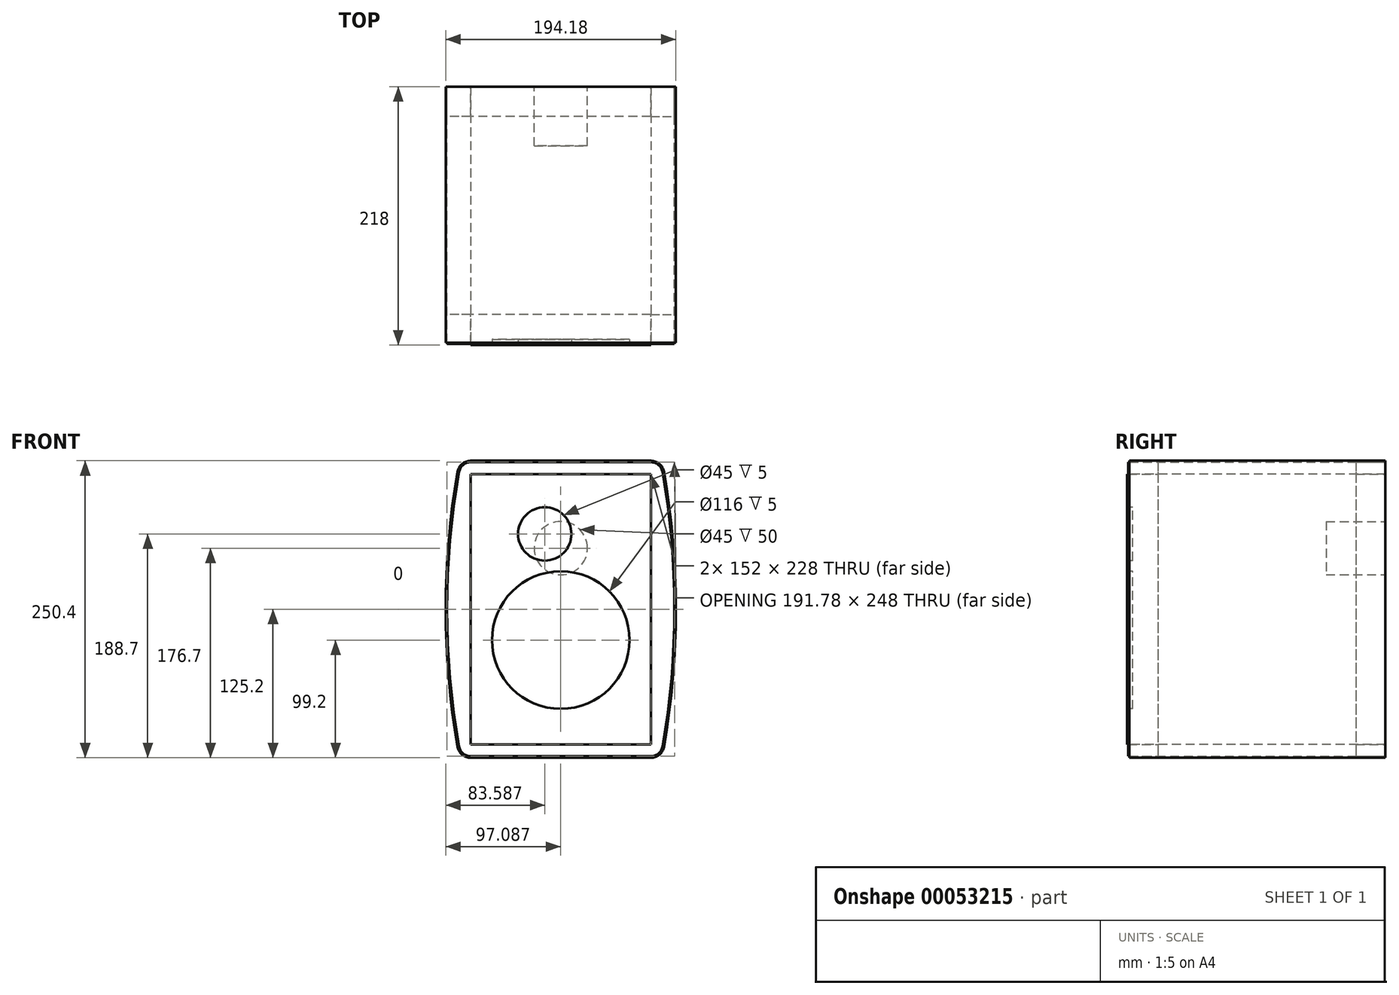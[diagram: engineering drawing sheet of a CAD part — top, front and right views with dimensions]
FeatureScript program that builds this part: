
annotation { "Feature Type Name" : "Feature", "Feature Type Description" : "" }
export const myFeature = defineFeature(function(context is Context, id is Id, definition is map)
    precondition{}
    {
        {
            var Q0;
            Q0=qCreatedBy(makeId("Top.planeOp"),FACE);
            var sketch = newSketch(context, id + "F0", { "sketchPlane" : qUnion([Q0])});
            skLineSegment(sketch, "E0.bottom", {"start": v(-73.3, 36.27) * mm, "end": v(78.7, 36.27) * mm});
            skLineSegment(sketch, "E0.top", {"start": v(-73.3, -181.73) * mm, "end": v(78.7, -181.73) * mm});
            skLineSegment(sketch, "E0.left", {"start": v(-73.3, 36.27) * mm, "end": v(-73.3, -181.73) * mm});
            skLineSegment(sketch, "E0.right", {"start": v(78.7, 36.27) * mm, "end": v(78.7, -181.73) * mm});
            skSolve(sketch);
        }
        {
            var Q0;
            Q0 = qSketchRegion(id + "F0", true);
            extrude(context, id + "F1", {"entities" : qUnion([Q0]), "depth" : 228 * mm});
        }
        {
            var Q0;
            Q0=makeQuery(id+"F1.opExtrude","SWEPT_FACE",FACE,{"disambiguationData":[OSD([sQuery(id+"F0.wireOp",EDGE,"E0.top")])]});
            var sketch = newSketch(context, id + "F2", { "sketchPlane" : qUnion([Q0])});
            skCircle(sketch, "E1", {"center": v(2.7, 88) * mm, "radius": 58 * mm});
            skCircle(sketch, "E2", {"center": v(-10.8, 177.5) * mm, "radius": 22.5 * mm});
            skSolve(sketch);
        }
        {
            var Q0;
            Q0 = qSketchRegion(id + "F2", true);
            extrude(context, id + "F3", {"entities" : qUnion([Q0]), "operationType" : NewBodyOperationType.REMOVE, "oppositeDirection" : true, "depth" : 5 * mm});
        }
        {
            var Q0;
            Q0=makeQuery(id+"F1.opExtrude","SWEPT_FACE",FACE,{"disambiguationData":[OSD([sQuery(id+"F0.wireOp",EDGE,"E0.bottom")])]});
            var sketch = newSketch(context, id + "F4", { "sketchPlane" : qUnion([Q0])});
            skCircle(sketch, "E3", {"center": v(-2.7, 165.5) * mm, "radius": 22.5 * mm});
            skSolve(sketch);
        }
        {
            var Q0;
            Q0=makeQuery(id+"F4.imprint","IMPRINT",FACE,{"disambiguationData":[TD([[makeQuery(id+"F4.imprint","IMPRINT",EDGE,{"derivedFrom":sQuery(id+"F4.wireOp",EDGE,"E3")}),1.0]])]});
            extrude(context, id + "F5", {"entities" : qUnion([Q0]), "operationType" : NewBodyOperationType.REMOVE, "oppositeDirection" : true, "depth" : 50 * mm});
        }
        {
            var Q0;
            Q0=makeQuery(id+"F1.opExtrude","SWEPT_FACE",FACE,{"disambiguationData":[OSD([sQuery(id+"F0.wireOp",EDGE,"E0.bottom")])]});
            var sketch = newSketch(context, id + "F6", { "sketchPlane" : qUnion([Q0])});
            skLineSegment(sketch, "E4", {"start": v(73.3, 114) * mm, "end": v(573.3, 114) * mm, "construction": true});
            skPoint(sketch, "E4.endSnap0", {"position": v(73.3, 114) * mm});
            skArc(sketch, "E5", {"start": v(-88.56, 229.72) * mm, "mid": v(-98.6, 114) * mm, "end": v(-88.56, -1.72) * mm});
            skLineSegment(sketch, "E6", {"start": v(-78.7, 238) * mm, "end": v(73.3, 238) * mm});
            skLineSegment(sketch, "E7", {"start": v(-2.7, 0) * mm, "end": v(-2.7, 228) * mm});
            skArc(sketch, "E8.MirrorCS", {"start": v(83.14, 229.72) * mm, "mid": v(93.18, 114) * mm, "end": v(83.14, -1.72) * mm});
            skLineSegment(sketch, "E9", {"start": v(-78.7, -10) * mm, "end": v(73.3, -10) * mm});
            skArc(sketch, "E10", {"start": v(-88.56, 229.72) * mm, "mid": v(-85.14, 235.66) * mm, "end": v(-78.7, 238) * mm});
            skArc(sketch, "E11", {"start": v(-88.56, -1.72) * mm, "mid": v(-85.14, -7.66) * mm, "end": v(-78.7, -10) * mm});
            skArc(sketch, "E12.MirrorCS", {"start": v(83.14, 229.72) * mm, "mid": v(79.73, 235.66) * mm, "end": v(73.3, 238) * mm});
            skArc(sketch, "E13.MirrorCS", {"start": v(83.14, -1.72) * mm, "mid": v(79.73, -7.66) * mm, "end": v(73.3, -10) * mm});
            skLineSegment(sketch, "E14.bottom", {"start": v(73.3, 228) * mm, "end": v(-78.7, 228) * mm});
            skLineSegment(sketch, "E14.top", {"start": v(73.3, 0) * mm, "end": v(-78.7, 0) * mm});
            skLineSegment(sketch, "E14.left", {"start": v(73.3, 228) * mm, "end": v(73.3, 0) * mm});
            skLineSegment(sketch, "E14.right", {"start": v(-78.7, 228) * mm, "end": v(-78.7, 0) * mm});
            skSolve(sketch);
        }
        {
            var Q0;
            Q0=makeQuery(id+"F6.imprint","IMPRINT",FACE,{"disambiguationData":[TD([[makeQuery(id+"F6.imprint","IMPRINT",EDGE,{"derivedFrom":sQuery(id+"F6.wireOp",EDGE,"E5")}),1.0]])]});
            extrude(context, id + "F7", {"entities" : qUnion([Q0]), "oppositeDirection" : true, "depth" : 25 * mm});
        }
        {
            var Q0;
            Q0=makeQuery(id+"F7.opExtrude","SWEPT_BODY",BODY,{"disambiguationData":[OSD([sQuery(id+"F6.wireOp",EDGE,"E5"),sQuery(id+"F6.wireOp",EDGE,"E6"),sQuery(id+"F6.wireOp",EDGE,"E8.MirrorCS"),sQuery(id+"F6.wireOp",EDGE,"E9"),sQuery(id+"F6.wireOp",EDGE,"E10"),sQuery(id+"F6.wireOp",EDGE,"E11"),sQuery(id+"F6.wireOp",EDGE,"E12.MirrorCS"),sQuery(id+"F6.wireOp",EDGE,"E13.MirrorCS"),sQuery(id+"F6.wireOp",EDGE,"E14.bottom"),sQuery(id+"F6.wireOp",EDGE,"E14.top"),sQuery(id+"F6.wireOp",EDGE,"E14.left"),sQuery(id+"F6.wireOp",EDGE,"E14.right")])]});
            transform(context, id + "F8", {"entities" : qUnion([Q0]), "transformType" : TransformType.TRANSLATION_3D, "dx" : 0 * mm, "dy" : -192 * mm, "dz" : 0 * mm, "makeCopy" : true});
        }
        {
            var Q0;
            Q0=makeQuery(id+"F1.opExtrude","SWEPT_FACE",FACE,{"disambiguationData":[OSD([sQuery(id+"F0.wireOp",EDGE,"E0.bottom")])]});
            var sketch = newSketch(context, id + "F9", { "sketchPlane" : qUnion([Q0])});
            skArc(sketch, "E15.0", {"start": v(-88.56, 229.72) * mm, "mid": v(-98.6, 114) * mm, "end": v(-88.56, -1.72) * mm});
            skArc(sketch, "E15.1", {"start": v(-88.56, 229.72) * mm, "mid": v(-85.14, 235.66) * mm, "end": v(-78.7, 238) * mm});
            skLineSegment(sketch, "E15.2", {"start": v(-78.7, 238) * mm, "end": v(73.3, 238) * mm});
            skArc(sketch, "E15.3", {"start": v(83.14, 229.72) * mm, "mid": v(79.73, 235.66) * mm, "end": v(73.3, 238) * mm});
            skArc(sketch, "E15.4", {"start": v(83.14, 229.72) * mm, "mid": v(93.18, 114) * mm, "end": v(83.14, -1.72) * mm});
            skArc(sketch, "E15.5", {"start": v(83.14, -1.72) * mm, "mid": v(79.73, -7.66) * mm, "end": v(73.3, -10) * mm});
            skLineSegment(sketch, "E15.6", {"start": v(-78.7, -10) * mm, "end": v(73.3, -10) * mm});
            skArc(sketch, "E15.7", {"start": v(-88.56, -1.72) * mm, "mid": v(-85.14, -7.66) * mm, "end": v(-78.7, -10) * mm});
            skArc(sketch, "E16.0", {"start": v(-89.74, 229.93) * mm, "mid": v(-85.91, 236.57) * mm, "end": v(-78.7, 239.2) * mm});
            skArc(sketch, "E16.1", {"start": v(-89.74, 229.93) * mm, "mid": v(-99.8, 114) * mm, "end": v(-89.74, -1.93) * mm});
            skLineSegment(sketch, "E16.2", {"start": v(-78.7, 239.2) * mm, "end": v(73.3, 239.2) * mm});
            skArc(sketch, "E16.3", {"start": v(-89.74, -1.93) * mm, "mid": v(-85.91, -8.57) * mm, "end": v(-78.7, -11.2) * mm});
            skArc(sketch, "E16.4", {"start": v(84.33, 229.93) * mm, "mid": v(80.5, 236.57) * mm, "end": v(73.3, 239.2) * mm});
            skArc(sketch, "E16.5", {"start": v(84.33, 229.93) * mm, "mid": v(94.38, 114) * mm, "end": v(84.33, -1.93) * mm});
            skArc(sketch, "E16.6", {"start": v(84.33, -1.93) * mm, "mid": v(80.5, -8.57) * mm, "end": v(73.3, -11.2) * mm});
            skLineSegment(sketch, "E16.7", {"start": v(-78.7, -11.2) * mm, "end": v(73.3, -11.2) * mm});
            skSolve(sketch);
        }
        {
            var Q0;
            Q0=makeQuery(id+"F9.imprint","IMPRINT",FACE,{"disambiguationData":[TD([[makeQuery(id+"F9.imprint","IMPRINT",EDGE,{"derivedFrom":sQuery(id+"F9.wireOp",EDGE,"E15.0")}),-1.0]])]});
            extrude(context, id + "F10", {"entities" : qUnion([Q0]), "oppositeDirection" : true, "depth" : 216 * mm});
        }
    });
